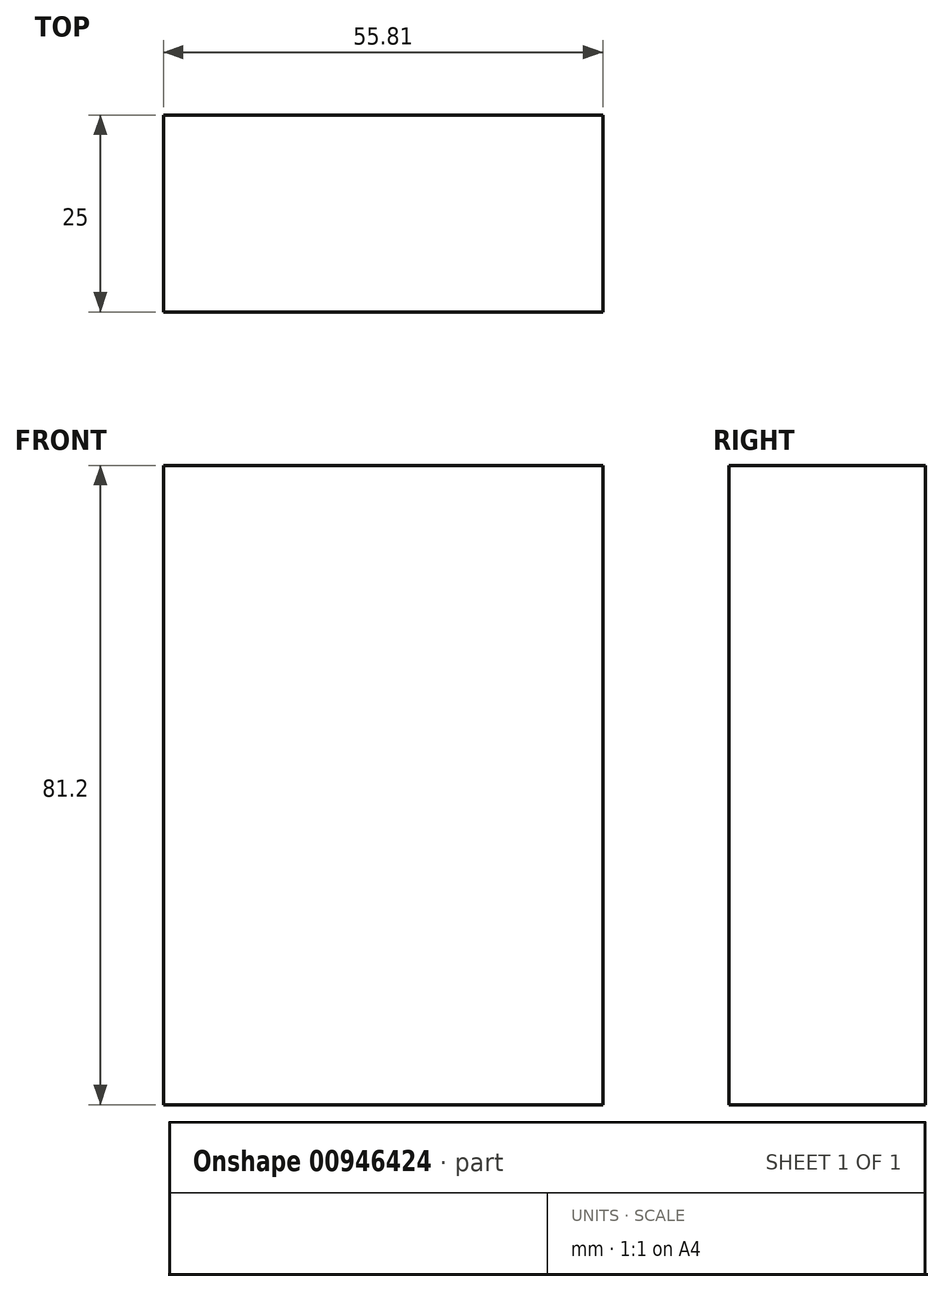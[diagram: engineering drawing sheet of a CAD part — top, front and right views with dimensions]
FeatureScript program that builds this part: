
annotation { "Feature Type Name" : "Feature", "Feature Type Description" : "" }
export const myFeature = defineFeature(function(context is Context, id is Id, definition is map)
    precondition{}
    {
        {
            var Q0;
            Q0=qCreatedBy(makeId("Front.planeOp"),FACE);
            var sketch = newSketch(context, id + "F0", { "sketchPlane" : qUnion([Q0])});
            skLineSegment(sketch, "E0.bottom", {"start": v(-89.86, 39.08) * mm, "end": v(-34.05, 39.08) * mm});
            skLineSegment(sketch, "E0.top", {"start": v(-89.86, -42.12) * mm, "end": v(-34.05, -42.12) * mm});
            skLineSegment(sketch, "E0.left", {"start": v(-89.86, 39.08) * mm, "end": v(-89.86, -42.12) * mm});
            skLineSegment(sketch, "E0.right", {"start": v(-34.05, 39.08) * mm, "end": v(-34.05, -42.12) * mm});
            skSolve(sketch);
        }
        {
            var Q0;
            Q0=makeQuery(id+"F0.imprint","IMPRINT",FACE,{"disambiguationData":[TD([[makeQuery(id+"F0.imprint","IMPRINT",EDGE,{"derivedFrom":sQuery(id+"F0.wireOp",EDGE,"E0.bottom")}),-1.0]])]});
            extrude(context, id + "F1", {"entities" : qUnion([Q0]), "depth" : 25 * mm, "offsetDistance" : 25 * mm});
        }
    });
